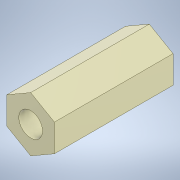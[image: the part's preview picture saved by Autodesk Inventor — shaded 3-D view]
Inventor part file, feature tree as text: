
AUTODESK INVENTOR PART (.ipt)
format: ipt  version: 2020.2 (Build 242310000, 310)  size: 99,328 bytes
history: native  units: mm
features: other x1, extrude x1, sketch x1
ambient origin geometry x8: Origin, YZ Plane, XZ Plane, XY Plane, X Axis, Y Axis, Z Axis, Center Point
bodies: Body1 (feature_tree)
feature tree (3):
  other  "ソリッド1"
  extrude  "押し出し1"  Depth=6.0mm
  sketch  "スケッチ1"
